# Revit family: QF_Marra Forni_ELST55-36_4
name_source: partatom
category: Specialty Equipment
revit_build: Autodesk Revit 2018 (Build: 20190510_1515(x64)
units: mm (PartAtom-declared; Revit-internal decimal feet)

## family parameters
Always vertical = Yes
Cut with Voids When Loaded = No
OmniClass Number = 23.40.40.14.17.11
OmniClass Title = Cookers, Ovens, Stoves
Part Type = Normal
Room Calculation Point = No
Round Connector Dimension = Use Diameter
Shared = No
Work Plane-Based = No

## types (1)
- QF_Marra Forni_ELST55-36_4
    Apparent Power = 57643 VA
    Assembly Code = E1090320
    CSI MasterFormat = 11 44 16
    Conn Conduit = Yes
    Cycle = 60 Hz
    Depth = 5' - 1 3/16"
    Description = Electric Stackable Deck Oven
    Elec Conn Connection Height = 0' - 4 9/32"
    Elec Conn RI Height = 0' - 0"
    Electric Connection Type = Direct
    Electrical Remarks = 50/60Hz Service Required, Requires Four (4) Seperate Electrical Connections Each At: 208V/60/3 - 40 Amps 14.6 kW, Connection Height: 4 17/64", 1' 7 23/64", 2' 10 29/64", 4' 1 35/64"
    Exhaust RI Height = 0' - 0"
    Exhaust Static Press = 0.04 in-wg
    Exhaust Vent Diameter = 0' - 8"
    Exhaust Volume = 520 CFM
    FL Amps = 160 A
    Foodservice Equipment Identifier = Yes
    Height = 6' - 5 13/32"
    Identify Quantity as Lot = Yes
    Manufacturer = Marra Forni
    Masterspec = Division 11
    Max Overcurrent Protection = 165 A
    Min Ckt Ampacity = 160 A
    Model = ELST55-36/4
    Number of Poles = 3
    Phase = 3
    Specification by Manufacturer = Marra Forni electric deck oven, four independent stacked cooking decks each with 55" x 36" MarraStone cooking surface, 250 -950 degrees F cooking range.  Heavy-duty Stainless Steel front and door panel construction.  MarraSmart digital programmable touchscreen control interface, independent radiant ceiling and deck temperature control, full-width window and cool to touch door handle, manual humidity evacuation damper, heavy duty spring and counter-balance doors, certified and approved for use with direct venting.  Requires mobile stand ESS55-36/4 (NOT INCLUDED). 208V/60Hz/3Ph/40amp ETL, ETL-NSF, ETL-CSA
    URL = https://marraforni.com
    URL Cutsheet = https://drive.google.com
    Volts = 208 V
    Watts = 58400 W
    Weight in Pounds = 3750
    Width = 5' - 10 19/32"

## geometry (parser evidence)
native form markers: Sweep x20
no freeform markers — native parametric forms only
